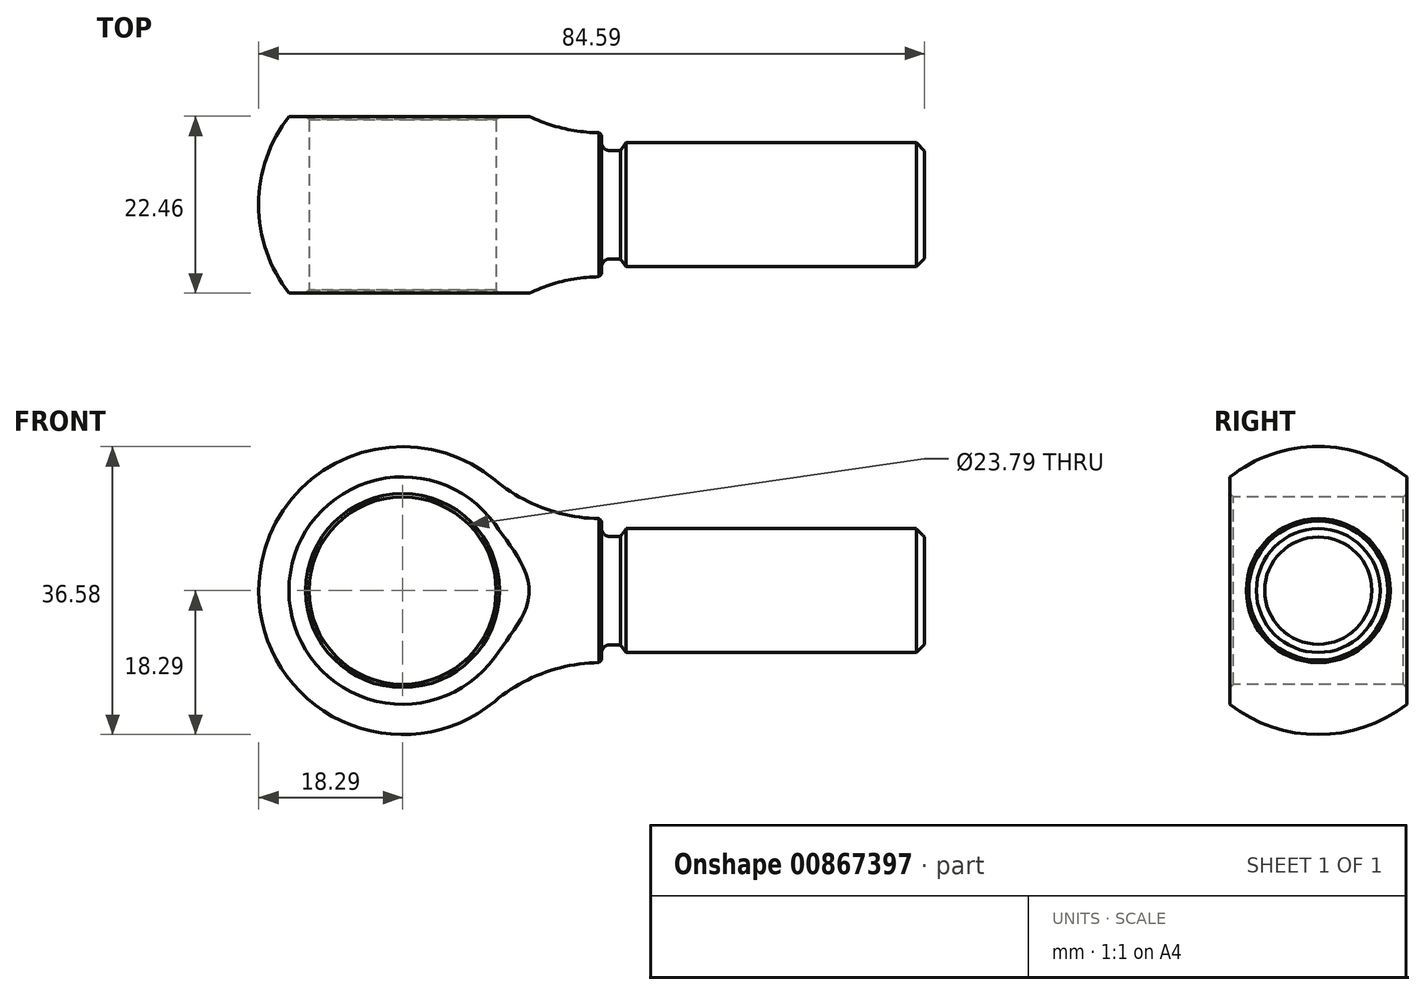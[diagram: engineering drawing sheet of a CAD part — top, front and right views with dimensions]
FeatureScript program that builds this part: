
annotation { "Feature Type Name" : "Feature", "Feature Type Description" : "" }
export const myFeature = defineFeature(function(context is Context, id is Id, definition is map)
    precondition{}
    {
        {
            var Q0;
            Q0=qCreatedBy(makeId("Front.planeOp"),FACE);
            var sketch = newSketch(context, id + "F0", { "sketchPlane" : qUnion([Q0])});
            skArc(sketch, "E0", {"start": v(14.07, 16.87) * mm, "mid": v(-9.32, 19.9) * mm, "end": v(-21.97, 0) * mm});
            skArc(sketch, "E1", {"start": v(14.07, 16.87) * mm, "mid": v(21.52, 12.56) * mm, "end": v(29.97, 10.99) * mm});
            skLineSegment(sketch, "E2", {"start": v(31.62, 8.25) * mm, "end": v(33.22, 8.25) * mm});
            skLineSegment(sketch, "E3", {"start": v(33.22, 8.25) * mm, "end": v(34.1, 9.45) * mm});
            skLineSegment(sketch, "E4", {"start": v(34.1, 9.45) * mm, "end": v(78.36, 9.45) * mm});
            skLineSegment(sketch, "E5", {"start": v(78.36, 9.45) * mm, "end": v(79.63, 8.18) * mm});
            skLineSegment(sketch, "E6", {"start": v(79.63, 8.18) * mm, "end": v(79.63, 0) * mm});
            skLineSegment(sketch, "E7", {"start": v(-21.97, 0) * mm, "end": v(79.63, 0) * mm, "construction": true});
            skArc(sketch, "E8", {"start": v(30.35, 9.52) * mm, "mid": v(30.72, 8.63) * mm, "end": v(31.62, 8.25) * mm});
            skLineSegment(sketch, "E9", {"start": v(30.35, 10.6) * mm, "end": v(30.35, 9.52) * mm});
            skLineSegment(sketch, "E10", {"start": v(29.97, 10.99) * mm, "end": v(30.35, 10.6) * mm});
            skPoint(sketch, "E11.orphan", {"position": v(30.35, 10.99) * mm});
            skLineSegment(sketch, "E12", {"start": v(-21.97, 0) * mm, "end": v(79.63, 0) * mm});
            skSolve(sketch);
        }
        {
            var Q0;
            Q0=makeQuery(id+"F0.imprint","IMPRINT",FACE,{"disambiguationData":[TD([[makeQuery(id+"F0.imprint","IMPRINT",EDGE,{"derivedFrom":sQuery(id+"F0.wireOp",EDGE,"E0")}),1.0]])]});
            var Q1;
            Q1=sQuery(id+"F0.wireOp",EDGE,"E12");
            revolve(context, id + "F1", {"surfaceOperationType" : NewSurfaceOperationType.NEW, "entities" : qUnion([Q0]), "axis" : qUnion([Q1]), "revolveType" : RevolveType.FULL});
        }
        {
            var Q0;
            Q0=qCreatedBy(makeId("Right.planeOp"),FACE);
            var sketch = newSketch(context, id + "F2", { "sketchPlane" : qUnion([Q0])});
            skLineSegment(sketch, "E13.bottom", {"start": v(13.49, 38.1) * mm, "end": v(-13.49, 38.1) * mm});
            skLineSegment(sketch, "E13.top", {"start": v(13.49, -38.1) * mm, "end": v(-13.49, -38.1) * mm});
            skLineSegment(sketch, "E13.left", {"start": v(13.49, 38.1) * mm, "end": v(13.49, -38.1) * mm});
            skLineSegment(sketch, "E13.right", {"start": v(-13.49, 38.1) * mm, "end": v(-13.49, -38.1) * mm});
            skPoint(sketch, "E13.middle", {"position": v(0, 0) * mm});
            skLineSegment(sketch, "E14.bottom", {"start": v(115.09, 139.7) * mm, "end": v(-115.09, 139.7) * mm});
            skLineSegment(sketch, "E14.top", {"start": v(115.09, -139.7) * mm, "end": v(-115.09, -139.7) * mm});
            skLineSegment(sketch, "E14.left", {"start": v(115.09, 139.7) * mm, "end": v(115.09, -139.7) * mm});
            skLineSegment(sketch, "E14.right", {"start": v(-115.09, 139.7) * mm, "end": v(-115.09, -139.7) * mm});
            skSolve(sketch);
        }
        {
            var Q0;
            Q0 = qSketchRegion(id + "F2", true);
            extrude(context, id + "F3", {"entities" : qUnion([Q0]), "operationType" : NewBodyOperationType.REMOVE, "endBound" : BoundingType.THROUGH_ALL, "oppositeDirection" : true, "depth" : 25.4 * mm, "offsetDistance" : 25.4 * mm, "hasSecondDirection" : true, "secondDirectionBound" : SecondDirectionBoundingType.THROUGH_ALL, "secondDirectionOppositeDirection" : false, "secondDirectionDepth" : 25.4 * mm});
        }
        {
            var Q0;
            Q0=qCreatedBy(makeId("Front.planeOp"),FACE);
            var sketch = newSketch(context, id + "F4", { "sketchPlane" : qUnion([Q0])});
            skCircle(sketch, "E15", {"center": v(0, 0) * mm, "radius": 14.29 * mm});
            skSolve(sketch);
        }
        {
            var Q0;
            Q0 = qSketchRegion(id + "F4", true);
            extrude(context, id + "F5", {"entities" : qUnion([Q0]), "operationType" : NewBodyOperationType.REMOVE, "endBound" : BoundingType.THROUGH_ALL, "oppositeDirection" : true, "depth" : 25.4 * mm, "offsetDistance" : 25.4 * mm, "hasSecondDirection" : true, "secondDirectionBound" : SecondDirectionBoundingType.THROUGH_ALL, "secondDirectionOppositeDirection" : false, "secondDirectionDepth" : 25.4 * mm});
        }
        {
            var Q0;
            Q0=makeQuery(id+"F5.boolean.opBoolean","INTERSECT",EDGE,{"derivedFrom":[makeQuery(id+"F3.boolean.opBoolean","COPY",FACE,{"derivedFrom":makeQuery(id+"F3.opExtrude","SWEPT_FACE",FACE,{"disambiguationData":[OSD([sQuery(id+"F2.wireOp",EDGE,"E13.left")])]})}),makeQuery(id+"F5.opExtrude","SWEPT_FACE",FACE,{"disambiguationData":[OSD([sQuery(id+"F4.wireOp",EDGE,"E15")])]})]});
            var Q1;
            Q1=makeQuery(id+"F5.boolean.opBoolean","INTERSECT",EDGE,{"derivedFrom":[makeQuery(id+"F3.boolean.opBoolean","COPY",FACE,{"derivedFrom":makeQuery(id+"F3.opExtrude","SWEPT_FACE",FACE,{"disambiguationData":[OSD([sQuery(id+"F2.wireOp",EDGE,"E13.right")])]})}),makeQuery(id+"F5.opExtrude","SWEPT_FACE",FACE,{"disambiguationData":[OSD([sQuery(id+"F4.wireOp",EDGE,"E15")])]})]});
            chamfer(context, id + "F6", {"entities" : qUnion([Q0, Q1]), "width" : 0.5 * mm, "tangentPropagation" : true});
        }
        {
            var Q0;
            Q0=makeQuery(id+"F1.opRevolve","SWEPT_BODY",BODY,{"disambiguationData":[OSD([sQuery(id+"F0.wireOp",EDGE,"E0"),sQuery(id+"F0.wireOp",EDGE,"E1"),sQuery(id+"F0.wireOp",EDGE,"E2"),sQuery(id+"F0.wireOp",EDGE,"E3"),sQuery(id+"F0.wireOp",EDGE,"E4"),sQuery(id+"F0.wireOp",EDGE,"E5"),sQuery(id+"F0.wireOp",EDGE,"E6"),sQuery(id+"F0.wireOp",EDGE,"E8"),sQuery(id+"F0.wireOp",EDGE,"E9"),sQuery(id+"F0.wireOp",EDGE,"E10"),sQuery(id+"F0.wireOp",EDGE,"E12")])]});
            var Q1;
            Q1=qCreatedBy(makeId("Origin.pointOp"),VERTEX);
            transform(context, id + "F7", {"entities" : qUnion([Q0]), "transformType" : TransformType.SCALE_UNIFORMLY, "scale" : .832549, "scalePoint" : qUnion([Q1]), "makeCopy" : false});
        }
    });
